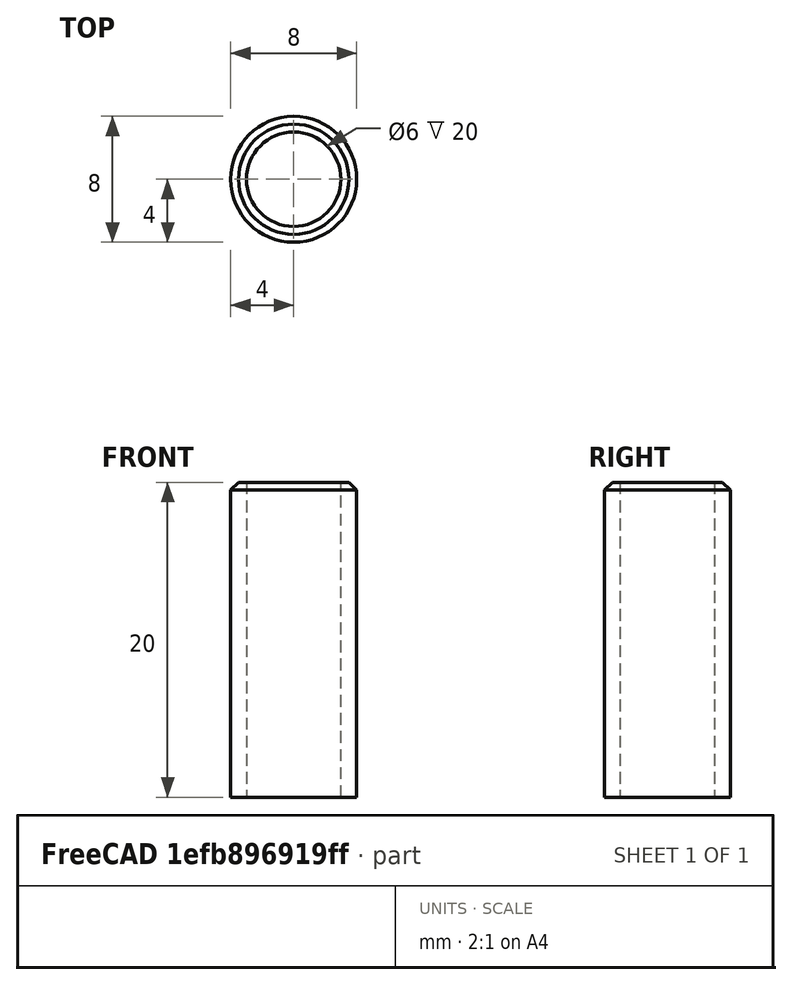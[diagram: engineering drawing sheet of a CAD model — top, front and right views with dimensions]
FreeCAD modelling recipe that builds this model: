
FCSTD DOCUMENT  (FreeCAD 0.19R24276 (Git))
Label: tube_d8
License: All rights reserved
LicenseURL: http://en.wikipedia.org/wiki/All_rights_reserved
objects: Sketcher::SketchObject×1, PartDesign::Pad×1, PartDesign::Chamfer×1, PartDesign::Body×1
note: 6 computed .brp shape members not serialized (recipe doc carries the construction recipe); baked Part::Feature solids carry a one-line shape summary decoded from their .brp

FEATURE [Sketcher::SketchObject] Sketch
  FullyConstrained = true
  MapMode = 5
  Support = -> [XY_Plane]
  sketch-geometry (2):
    g0: Circle CenterX=0 CenterY=0 CenterZ=0 NormalX=0 NormalY=0 NormalZ=1 AngleXU=0 Radius=4
    g1: Circle CenterX=0 CenterY=0 CenterZ=0 NormalX=0 NormalY=0 NormalZ=1 AngleXU=0 Radius=3
  constraints (4):
    c: Coincident(g0,g-1)
    c: Diameter(g0) = 8
    c: Coincident(g1,g0)
    c: Diameter(g1) = 6
FEATURE [PartDesign::Pad] Pad
  Direction = (1,1,1)
  Length = 20
  Length2 = 100
  Profile = -> Sketch
  Type = 0
FEATURE [PartDesign::Chamfer] Chamfer
  Angle = 45
  Base = -> Pad [Edge3]
  BaseFeature = -> Pad
  ChamferType = 0
  FlipDirection = false
  Size = 0.5
  Size2 = 1
  SupportTransform = false
FEATURE [PartDesign::Body] Body
  Group = -> [Sketch,Pad,Chamfer]
  Origin = -> Origin
  Tip = -> Chamfer
